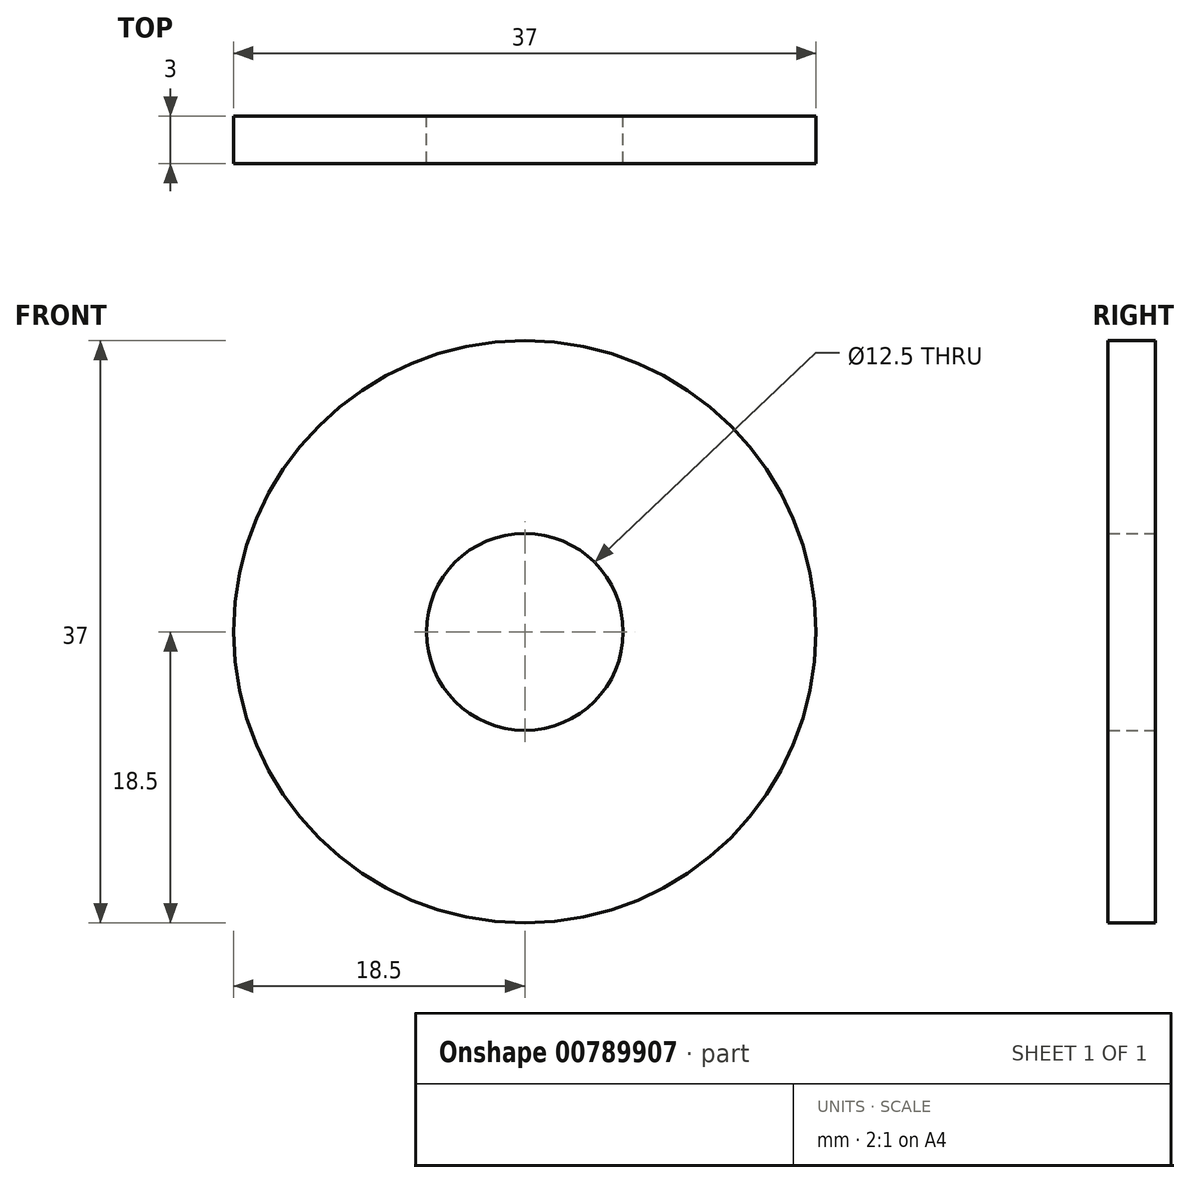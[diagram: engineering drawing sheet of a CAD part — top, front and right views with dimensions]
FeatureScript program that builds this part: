
annotation { "Feature Type Name" : "Feature", "Feature Type Description" : "" }
export const myFeature = defineFeature(function(context is Context, id is Id, definition is map)
    precondition{}
    {
        {
            var Q0;
            Q0=qCreatedBy(makeId("Front.planeOp"),FACE);
            var sketch = newSketch(context, id + "F0", { "sketchPlane" : qUnion([Q0])});
            skCircle(sketch, "E0", {"center": v(0, 0) * mm, "radius": 18.5 * mm});
            skCircle(sketch, "E1", {"center": v(0, 0) * mm, "radius": 6.25 * mm});
            skSolve(sketch);
        }
        {
            var Q0;
            Q0=qSketchRegion(id+"F0",true);
            extrude(context, id + "F1", {"entities" : qUnion([Q0]), "depth" : 3 * mm, "offsetDistance" : 25 * mm});
        }
    });
